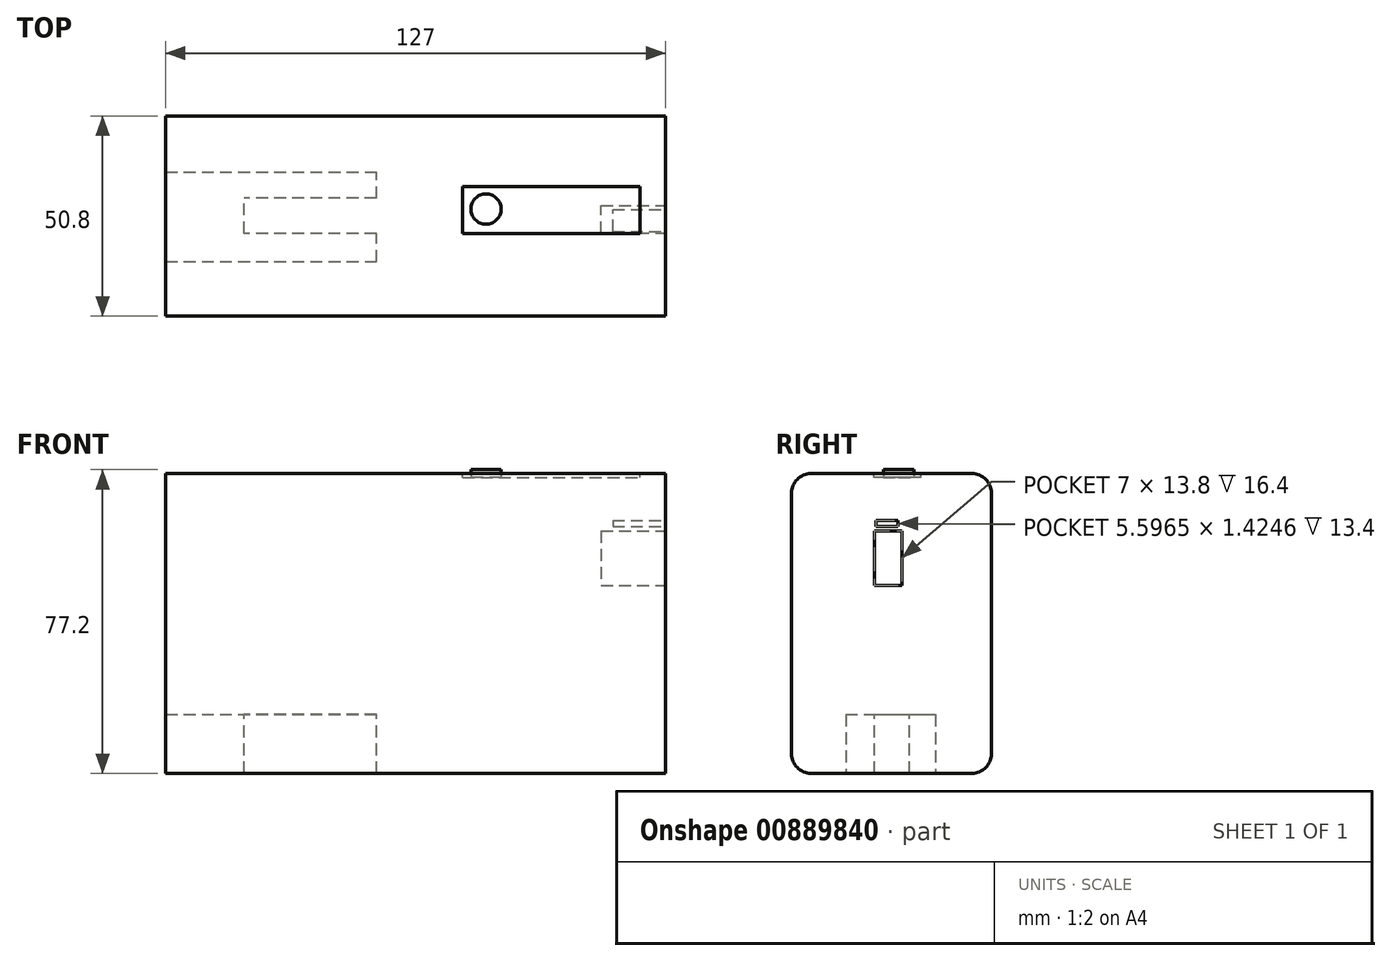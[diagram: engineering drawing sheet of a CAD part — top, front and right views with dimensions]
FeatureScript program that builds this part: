
annotation { "Feature Type Name" : "Feature", "Feature Type Description" : "" }
export const myFeature = defineFeature(function(context is Context, id is Id, definition is map)
    precondition{}
    {
        {
            var Q0;
            Q0=qCreatedBy(makeId("Front.planeOp"),FACE);
            var sketch = newSketch(context, id + "F0", { "sketchPlane" : qUnion([Q0])});
            skLineSegment(sketch, "E0.bottom", {"start": v(-63.5, -38.1) * mm, "end": v(63.5, -38.1) * mm});
            skLineSegment(sketch, "E0.top", {"start": v(-63.5, 38.1) * mm, "end": v(63.5, 38.1) * mm});
            skLineSegment(sketch, "E0.left", {"start": v(-63.5, -38.1) * mm, "end": v(-63.5, 38.1) * mm});
            skLineSegment(sketch, "E0.right", {"start": v(63.5, -38.1) * mm, "end": v(63.5, 38.1) * mm});
            skPoint(sketch, "E0.middle", {"position": v(0, 0) * mm});
            skSolve(sketch);
        }
        {
            var Q0;
            Q0 = qSketchRegion(id + "F0", true);
            extrude(context, id + "F1", {"entities" : qUnion([Q0]), "depth" : 50.8 * mm, "offsetDistance" : 25.4 * mm});
        }
        {
            var Q0;
            Q0=makeQuery(id+"F1.opExtrude","CAP_EDGE",EDGE,{"disambiguationData":[OSD([sQuery(id+"F0.wireOp",EDGE,"E0.top")])],"isStart":false});
            fillet(context, id + "F2", {"entities" : qUnion([Q0]), "radius" : 5 * mm, "tangentPropagation" : true, "allowEdgeOverflow" : false});
        }
        {
            var Q0;
            Q0=makeQuery(id+"F1.opExtrude","CAP_EDGE",EDGE,{"disambiguationData":[OSD([sQuery(id+"F0.wireOp",EDGE,"E0.top")])],"isStart":true});
            fillet(context, id + "F3", {"entities" : qUnion([Q0]), "radius" : 5 * mm, "tangentPropagation" : true, "allowEdgeOverflow" : false});
        }
        {
            var Q0;
            Q0=makeQuery(id+"F1.opExtrude","CAP_EDGE",EDGE,{"disambiguationData":[OSD([sQuery(id+"F0.wireOp",EDGE,"E0.bottom")])],"isStart":false});
            var Q1;
            Q1=makeQuery(id+"F1.opExtrude","CAP_EDGE",EDGE,{"disambiguationData":[OSD([sQuery(id+"F0.wireOp",EDGE,"E0.bottom")])],"isStart":true});
            fillet(context, id + "F4", {"entities" : qUnion([Q0, Q1]), "radius" : 5 * mm, "tangentPropagation" : true, "allowEdgeOverflow" : false});
        }
        {
            var Q0;
            Q0=makeQuery(id+"F1.opExtrude","SWEPT_FACE",FACE,{"disambiguationData":[OSD([sQuery(id+"F0.wireOp",EDGE,"E0.right")])]});
            var sketch = newSketch(context, id + "F5", { "sketchPlane" : qUnion([Q0])});
            skLineSegment(sketch, "E1.bottom", {"start": v(-29.76, 23.5) * mm, "end": v(-22.76, 23.5) * mm});
            skLineSegment(sketch, "E1.top", {"start": v(-29.76, 9.7) * mm, "end": v(-22.76, 9.7) * mm});
            skLineSegment(sketch, "E1.left", {"start": v(-29.76, 23.5) * mm, "end": v(-29.76, 9.7) * mm});
            skLineSegment(sketch, "E1.right", {"start": v(-22.76, 23.5) * mm, "end": v(-22.76, 9.7) * mm});
            skSolve(sketch);
        }
        {
            var Q0;
            Q0 = qSketchRegion(id + "F5", true);
            extrude(context, id + "F6", {"entities" : qUnion([Q0]), "operationType" : NewBodyOperationType.REMOVE, "oppositeDirection" : true, "depth" : 16.4 * mm, "offsetDistance" : 25.4 * mm});
        }
        {
            var Q0;
            Q0=makeQuery(id+"F1.opExtrude","SWEPT_FACE",FACE,{"disambiguationData":[OSD([sQuery(id+"F0.wireOp",EDGE,"E0.right")])]});
            var sketch = newSketch(context, id + "F7", { "sketchPlane" : qUnion([Q0])});
            skLineSegment(sketch, "E2.bottom", {"start": v(-29.3, 26.11) * mm, "end": v(-23.7, 26.11) * mm});
            skLineSegment(sketch, "E2.top", {"start": v(-29.3, 24.69) * mm, "end": v(-23.7, 24.69) * mm});
            skLineSegment(sketch, "E2.left", {"start": v(-29.3, 26.11) * mm, "end": v(-29.3, 24.69) * mm});
            skLineSegment(sketch, "E2.right", {"start": v(-23.7, 26.11) * mm, "end": v(-23.7, 24.69) * mm});
            skSolve(sketch);
        }
        {
            var Q0;
            Q0=makeQuery(id+"F7.imprint","IMPRINT",FACE,{"disambiguationData":[TD([[makeQuery(id+"F7.imprint","IMPRINT",EDGE,{"derivedFrom":sQuery(id+"F7.wireOp",EDGE,"E2.bottom")}),-1.0]])]});
            extrude(context, id + "F8", {"entities" : qUnion([Q0]), "operationType" : NewBodyOperationType.REMOVE, "oppositeDirection" : true, "depth" : 13.4 * mm, "offsetDistance" : 25.4 * mm});
        }
        {
            var Q0;
            Q0=makeQuery(id+"F1.opExtrude","SWEPT_FACE",FACE,{"disambiguationData":[OSD([sQuery(id+"F0.wireOp",EDGE,"E0.top")])]});
            var sketch = newSketch(context, id + "F9", { "sketchPlane" : qUnion([Q0])});
            skLineSegment(sketch, "E3.bottom", {"start": v(11.97, -17.89) * mm, "end": v(56.97, -17.89) * mm});
            skLineSegment(sketch, "E3.top", {"start": v(11.97, -29.89) * mm, "end": v(56.97, -29.89) * mm});
            skLineSegment(sketch, "E3.left", {"start": v(11.97, -17.89) * mm, "end": v(11.97, -29.89) * mm});
            skLineSegment(sketch, "E3.right", {"start": v(56.97, -17.89) * mm, "end": v(56.97, -29.89) * mm});
            skLineSegment(sketch, "E4.0.0", {"start": v(63.5, -45.8) * mm, "end": v(63.5, -5) * mm});
            skLineSegment(sketch, "E4.0.1", {"start": v(63.5, -5) * mm, "end": v(-63.5, -5) * mm});
            skLineSegment(sketch, "E4.0.2", {"start": v(-63.5, -5) * mm, "end": v(-63.5, -45.8) * mm});
            skLineSegment(sketch, "E4.0.3", {"start": v(-63.5, -45.8) * mm, "end": v(63.5, -45.8) * mm});
            skSolve(sketch);
        }
        {
            var Q0;
            Q0=makeQuery(id+"F9.imprint","IMPRINT",FACE,{"disambiguationData":[TD([[makeQuery(id+"F9.imprint","IMPRINT",EDGE,{"derivedFrom":sQuery(id+"F9.wireOp",EDGE,"E3.bottom")}),-1.0]])]});
            extrude(context, id + "F10", {"entities" : qUnion([Q0]), "operationType" : NewBodyOperationType.REMOVE, "oppositeDirection" : true, "depth" : 1 * mm, "offsetDistance" : 25.4 * mm});
        }
        {
            var Q0;
            Q0=makeQuery(id+"F10.boolean.opBoolean","COPY",FACE,{"derivedFrom":makeQuery(id+"F10.opExtrude","CAP_FACE",FACE,{"disambiguationData":[OSD([sQuery(id+"F9.wireOp",EDGE,"E3.bottom"),sQuery(id+"F9.wireOp",EDGE,"E3.top"),sQuery(id+"F9.wireOp",EDGE,"E3.left"),sQuery(id+"F9.wireOp",EDGE,"E3.right")])],"isStart":false})});
            var sketch = newSketch(context, id + "F11", { "sketchPlane" : qUnion([Q0])});
            skCircle(sketch, "E5", {"center": v(17.89, -23.62) * mm, "radius": 3.86 * mm});
            skSolve(sketch);
        }
        {
            var Q0;
            Q0=makeQuery(id+"F11.imprint","IMPRINT",FACE,{"disambiguationData":[TD([[makeQuery(id+"F11.imprint","IMPRINT",EDGE,{"derivedFrom":sQuery(id+"F11.wireOp",EDGE,"E5")}),1.0]])]});
            extrude(context, id + "F12", {"entities" : qUnion([Q0]), "operationType" : NewBodyOperationType.ADD, "depth" : 2 * mm, "offsetDistance" : 25.4 * mm});
        }
        {
            var Q0;
            Q0=makeQuery(id+"F1.opExtrude","SWEPT_FACE",FACE,{"disambiguationData":[OSD([sQuery(id+"F0.wireOp",EDGE,"E0.bottom")])]});
            var sketch = newSketch(context, id + "F13", { "sketchPlane" : qUnion([Q0])});
            skLineSegment(sketch, "E6.bottom", {"start": v(-63.5, 36.98) * mm, "end": v(-9.93, 36.98) * mm});
            skLineSegment(sketch, "E6.top", {"start": v(-63.5, 14.25) * mm, "end": v(-9.93, 14.25) * mm});
            skLineSegment(sketch, "E6.left", {"start": v(-63.5, 36.98) * mm, "end": v(-63.5, 14.25) * mm});
            skLineSegment(sketch, "E6.right", {"start": v(-9.93, 36.98) * mm, "end": v(-9.93, 14.25) * mm});
            skSolve(sketch);
        }
        {
            var Q0;
            Q0 = qSketchRegion(id + "F13", true);
            var Q1;
            Q1=makeQuery(id+"F13.imprint","IMPRINT",FACE,{"disambiguationData":[TD([[makeQuery(id+"F13.imprint","IMPRINT",EDGE,{"derivedFrom":sQuery(id+"F13.wireOp",EDGE,"E6.bottom")}),-1.0]])]});
            extrude(context, id + "F14", {"entities" : qUnion([Q0, Q1]), "operationType" : NewBodyOperationType.REMOVE, "oppositeDirection" : true, "depth" : 15 * mm, "offsetDistance" : 25.4 * mm});
        }
        {
            var Q0;
            Q0=makeQuery(id+"F14.boolean.opBoolean","COPY",FACE,{"derivedFrom":makeQuery(id+"F14.opExtrude","CAP_FACE",FACE,{"disambiguationData":[OSD([sQuery(id+"F13.wireOp",EDGE,"E6.bottom"),sQuery(id+"F13.wireOp",EDGE,"E6.top"),sQuery(id+"F13.wireOp",EDGE,"E6.left"),sQuery(id+"F13.wireOp",EDGE,"E6.right")])],"isStart":false})});
            var sketch = newSketch(context, id + "F15", { "sketchPlane" : qUnion([Q0])});
            skLineSegment(sketch, "E7.bottom", {"start": v(-9.93, 29.79) * mm, "end": v(-43.6, 29.79) * mm});
            skLineSegment(sketch, "E7.top", {"start": v(-9.93, 20.87) * mm, "end": v(-43.6, 20.87) * mm});
            skLineSegment(sketch, "E7.left", {"start": v(-9.93, 29.79) * mm, "end": v(-9.93, 20.87) * mm});
            skLineSegment(sketch, "E7.right", {"start": v(-43.6, 29.79) * mm, "end": v(-43.6, 20.87) * mm});
            skSolve(sketch);
        }
        {
            var Q0;
            Q0=makeQuery(id+"F15.imprint","IMPRINT",FACE,{"disambiguationData":[TD([[makeQuery(id+"F15.imprint","IMPRINT",EDGE,{"derivedFrom":sQuery(id+"F15.wireOp",EDGE,"E7.bottom")}),1.0]])]});
            extrude(context, id + "F16", {"entities" : qUnion([Q0]), "operationType" : NewBodyOperationType.ADD, "depth" : 15 * mm, "offsetDistance" : 25.4 * mm});
        }
    });
